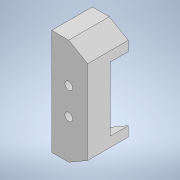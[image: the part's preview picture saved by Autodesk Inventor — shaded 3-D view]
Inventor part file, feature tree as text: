
AUTODESK INVENTOR PART (.ipt)
format: ipt  version: 2022 (Build 260153000, 153)  size: 119,808 bytes
history: native  units: in
note: dims shown in document units (in); Inventor stores cm internally (conversion verified against a paired STEP export)
features: extrude x2
ambient origin geometry x8: Origin, YZ Plane, XZ Plane, XY Plane, X Axis, Y Axis, Z Axis, Center Point
bodies: Solid1 (feature_tree)
feature tree (2):
  extrude  "Extrusion1"  Depth=0.374in
  extrude  "Extrusion2"  Depth=0.1063in
